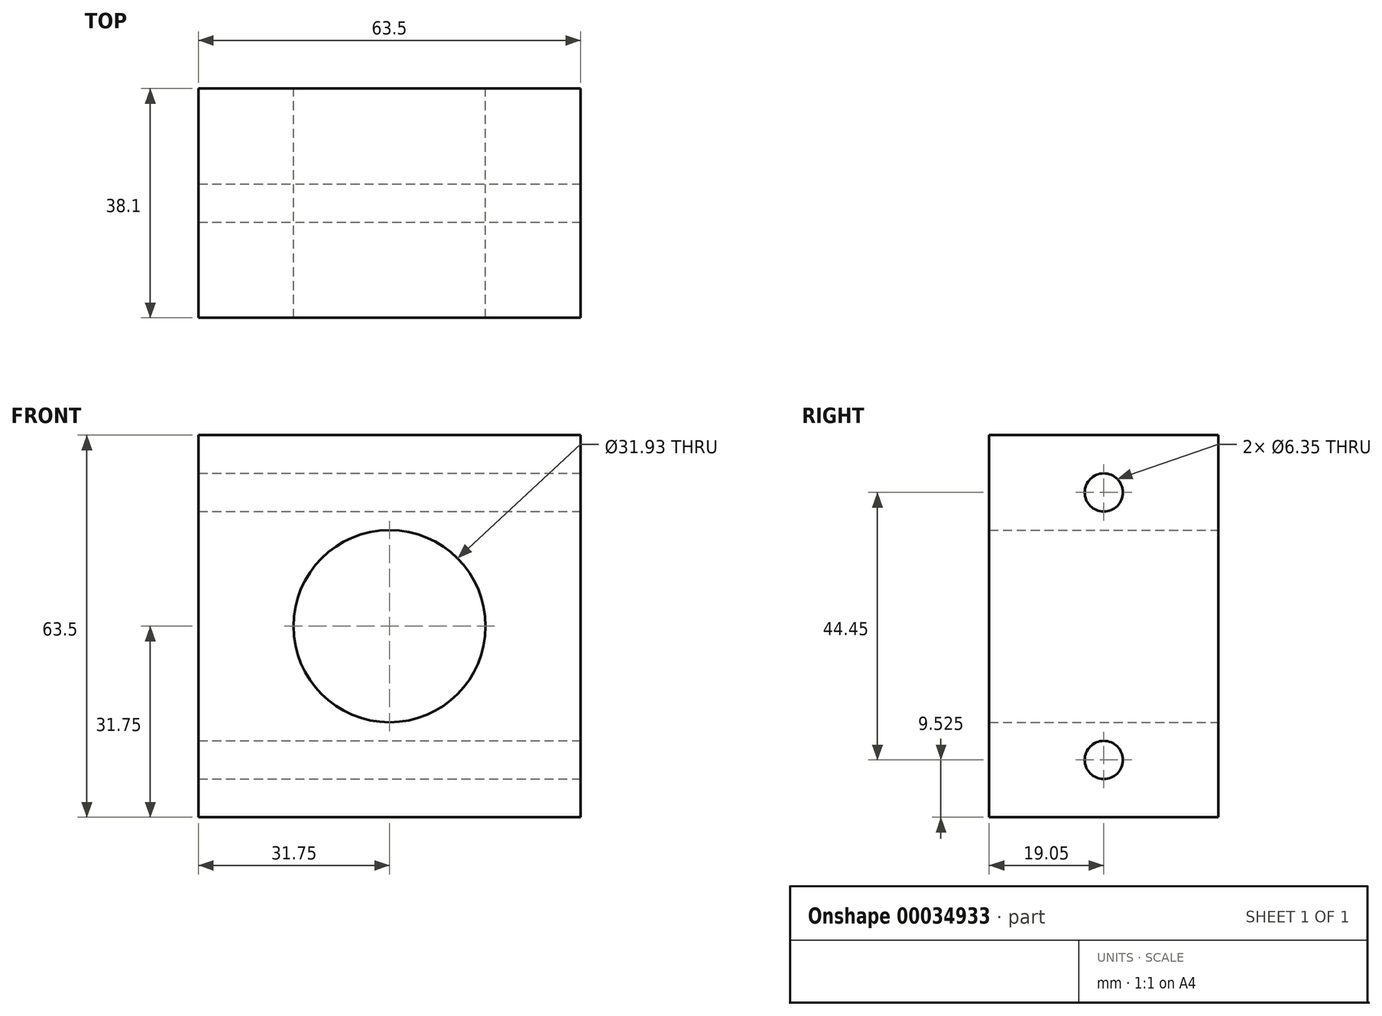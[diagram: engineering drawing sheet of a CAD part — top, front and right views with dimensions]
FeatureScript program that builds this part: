
annotation { "Feature Type Name" : "Feature", "Feature Type Description" : "" }
export const myFeature = defineFeature(function(context is Context, id is Id, definition is map)
    precondition{}
    {
        {
            var Q0;
            Q0=qCreatedBy(makeId("Front.planeOp"),FACE);
            var sketch = newSketch(context, id + "F0", { "sketchPlane" : qUnion([Q0])});
            skLineSegment(sketch, "E0.rect.bottom", {"start": v(31.75, 31.75) * mm, "end": v(-31.75, 31.75) * mm});
            skLineSegment(sketch, "E0.rect.top", {"start": v(31.75, -31.75) * mm, "end": v(-31.75, -31.75) * mm});
            skLineSegment(sketch, "E0.rect.left", {"start": v(31.75, 31.75) * mm, "end": v(31.75, -31.75) * mm});
            skLineSegment(sketch, "E0.rect.right", {"start": v(-31.75, 31.75) * mm, "end": v(-31.75, -31.75) * mm});
            skPoint(sketch, "E0.rect.middle", {"position": v(0, 0) * mm});
            skCircle(sketch, "E1", {"center": v(0, 0) * mm, "radius": 15.96 * mm});
            skSolve(sketch);
        }
        {
            var Q0;
            Q0 = qSketchRegion(id + "F0", true);
            extrude(context, id + "F1", {"entities" : qUnion([Q0]), "endBound" : BoundingType.SYMMETRIC, "depth" : 38.1 * mm});
        }
        {
            var Q0;
            Q0=qCreatedBy(makeId("Right.planeOp"),FACE);
            var sketch = newSketch(context, id + "F2", { "sketchPlane" : qUnion([Q0])});
            skCircle(sketch, "E2", {"center": v(0, 22.23) * mm, "radius": 3.18 * mm});
            skCircle(sketch, "E3.MirrorC", {"center": v(0, -22.23) * mm, "radius": 3.18 * mm});
            skSolve(sketch);
        }
        {
            var Q0;
            Q0 = qSketchRegion(id + "F2", true);
            extrude(context, id + "F3", {"entities" : qUnion([Q0]), "operationType" : NewBodyOperationType.REMOVE, "endBound" : BoundingType.SYMMETRIC, "oppositeDirection" : true, "depth" : 69.85 * mm});
        }
    });
